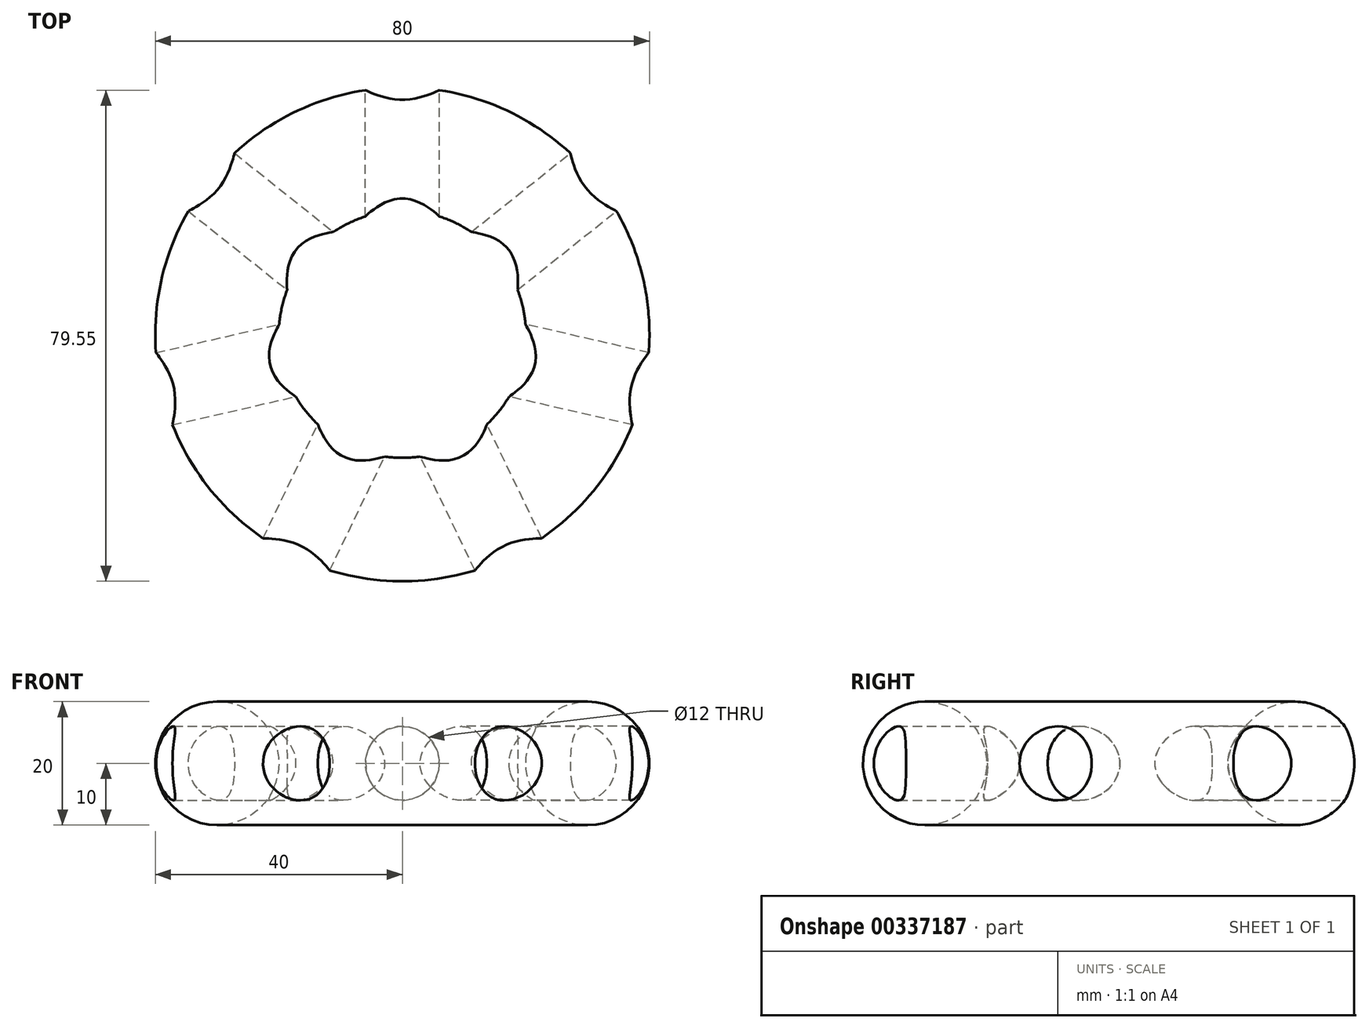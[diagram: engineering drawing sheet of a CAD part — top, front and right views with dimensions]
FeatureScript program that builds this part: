
annotation { "Feature Type Name" : "Feature", "Feature Type Description" : "" }
export const myFeature = defineFeature(function(context is Context, id is Id, definition is map)
    precondition{}
    {
        {
            var Q0;
            Q0=qCreatedBy(makeId("Front.planeOp"),FACE);
            var sketch = newSketch(context, id + "F0", { "sketchPlane" : qUnion([Q0])});
            skCircle(sketch, "E0", {"center": v(-30, 0) * mm, "radius": 10 * mm});
            skLineSegment(sketch, "E1", {"start": v(0, 0) * mm, "end": v(0, 40) * mm});
            skLineSegment(sketch, "E2", {"start": v(0, 0) * mm, "end": v(0, -40) * mm});
            skSolve(sketch);
        }
        {
            var Q0;
            Q0=makeQuery(id+"F0.imprint","IMPRINT",FACE,{"disambiguationData":[TD([[makeQuery(id+"F0.imprint","IMPRINT",EDGE,{"derivedFrom":sQuery(id+"F0.wireOp",EDGE,"E0")}),1.0]])]});
            var Q1;
            Q1=sQuery(id+"F0.wireOp",EDGE,"E1");
            revolve(context, id + "F1", {"entities" : qUnion([Q0]), "axis" : qUnion([Q1]), "revolveType" : RevolveType.FULL});
        }
        {
            var Q0;
            Q0=qCreatedBy(makeId("Top.planeOp"),FACE);
            var sketch = newSketch(context, id + "F2", { "sketchPlane" : qUnion([Q0])});
            skCircle(sketch, "E3", {"center": v(0, 0) * mm, "radius": 40 * mm});
            skLineSegment(sketch, "E4", {"start": v(0, 40) * mm, "end": v(0, 0) * mm});
            skLineSegment(sketch, "E5.1.0", {"start": v(-31.27, 24.94) * mm, "end": v(0, 0) * mm});
            skLineSegment(sketch, "E5.2.0", {"start": v(-39, -8.9) * mm, "end": v(0, 0) * mm});
            skLineSegment(sketch, "E6.1.3.0", {"start": v(-17.36, -36.04) * mm, "end": v(0, 0) * mm});
            skLineSegment(sketch, "E6.1.4.0", {"start": v(17.36, -36.04) * mm, "end": v(0, 0) * mm});
            skLineSegment(sketch, "E6.1.5.0", {"start": v(39, -8.9) * mm, "end": v(0, 0) * mm});
            skLineSegment(sketch, "E6.1.6.0", {"start": v(31.27, 24.94) * mm, "end": v(0, 0) * mm});
            skLineSegment(sketch, "E7.bottom", {"start": v(0, 40) * mm, "end": v(-6, 40) * mm});
            skLineSegment(sketch, "E7.top", {"start": v(0, 15) * mm, "end": v(-6, 15) * mm});
            skLineSegment(sketch, "E7.left", {"start": v(0, 40) * mm, "end": v(0, 15) * mm});
            skLineSegment(sketch, "E7.right", {"start": v(-6, 40) * mm, "end": v(-6, 15) * mm});
            skLineSegment(sketch, "E8.bottom", {"start": v(0, 40) * mm, "end": v(6, 40) * mm});
            skLineSegment(sketch, "E8.top", {"start": v(0, 15) * mm, "end": v(6, 15) * mm});
            skLineSegment(sketch, "E8.right", {"start": v(6, 40) * mm, "end": v(6, 15) * mm});
            skLineSegment(sketch, "E9.1.0", {"start": v(-27.53, 29.63) * mm, "end": v(-7.99, 14.04) * mm});
            skLineSegment(sketch, "E9.2.0", {"start": v(-40.33, -3.05) * mm, "end": v(-15.96, 2.51) * mm});
            skLineSegment(sketch, "E10.2.3.0", {"start": v(-22.76, -33.44) * mm, "end": v(-11.91, -10.91) * mm});
            skLineSegment(sketch, "E10.2.4.0", {"start": v(11.95, -38.64) * mm, "end": v(1.1, -16.12) * mm});
            skLineSegment(sketch, "E10.2.5.0", {"start": v(37.66, -14.75) * mm, "end": v(13.29, -9.19) * mm});
            skLineSegment(sketch, "E10.2.6.0", {"start": v(35.01, 20.25) * mm, "end": v(15.47, 4.66) * mm});
            skLineSegment(sketch, "E11", {"start": v(-27.53, 29.63) * mm, "end": v(-31.27, 24.94) * mm});
            skLineSegment(sketch, "E12", {"start": v(-7.99, 14.04) * mm, "end": v(-11.73, 9.35) * mm});
            skLineSegment(sketch, "E13", {"start": v(-15.96, 2.51) * mm, "end": v(-14.62, -3.34) * mm});
            skLineSegment(sketch, "E14", {"start": v(-11.91, -10.91) * mm, "end": v(-6.5, -13.51) * mm});
            skLineSegment(sketch, "E15", {"start": v(1.1, -16.12) * mm, "end": v(6.5, -13.51) * mm});
            skLineSegment(sketch, "E16", {"start": v(13.29, -9.19) * mm, "end": v(14.62, -3.34) * mm});
            skLineSegment(sketch, "E17", {"start": v(15.47, 4.66) * mm, "end": v(11.73, 9.35) * mm});
            skLineSegment(sketch, "E18", {"start": v(37.66, -14.75) * mm, "end": v(39, -8.9) * mm});
            skLineSegment(sketch, "E19", {"start": v(35.01, 20.25) * mm, "end": v(31.27, 24.94) * mm});
            skLineSegment(sketch, "E20", {"start": v(-39, -8.9) * mm, "end": v(-40.33, -3.05) * mm});
            skLineSegment(sketch, "E21", {"start": v(-17.36, -36.04) * mm, "end": v(-22.76, -33.44) * mm});
            skSolve(sketch);
        }
        {
            var Q0;
            {var subQ3=sQuery(id+"F2.wireOp",EDGE,"E17");Q0=makeQuery(id+"F2.imprint","IMPRINT",FACE,{"disambiguationData":[TD([[makeQuery(id+"F2.imprint","IMPRINT",EDGE,{"derivedFrom":subQ3}),-1.0]])]});}
            var Q1;
            Q1=sQuery(id+"F2.wireOp",EDGE,"E6.1.6.0");
            revolve(context, id + "F3", {"operationType" : NewBodyOperationType.REMOVE, "entities" : qUnion([Q0]), "axis" : qUnion([Q1]), "revolveType" : RevolveType.FULL});
        }
        {
            var Q0;
            {var subQ4=sQuery(id+"F2.wireOp",EDGE,"E8.top");Q0=makeQuery(id+"F2.imprint","IMPRINT",FACE,{"disambiguationData":[TD([[makeQuery(id+"F2.imprint","IMPRINT",EDGE,{"derivedFrom":subQ4}),1.0]])]});}
            var Q1;
            Q1=sQuery(id+"F2.wireOp",EDGE,"E4");
            revolve(context, id + "F4", {"operationType" : NewBodyOperationType.REMOVE, "entities" : qUnion([Q0]), "axis" : qUnion([Q1]), "revolveType" : RevolveType.FULL});
        }
        {
            var Q0;
            {var subQ3=sQuery(id+"F2.wireOp",EDGE,"E12");Q0=makeQuery(id+"F2.imprint","IMPRINT",FACE,{"disambiguationData":[TD([[makeQuery(id+"F2.imprint","IMPRINT",EDGE,{"derivedFrom":subQ3}),-1.0]])]});}
            var Q1;
            Q1=sQuery(id+"F2.wireOp",EDGE,"E5.1.0");
            revolve(context, id + "F5", {"operationType" : NewBodyOperationType.REMOVE, "entities" : qUnion([Q0]), "axis" : qUnion([Q1]), "revolveType" : RevolveType.FULL, "oppositeDirection" : true});
        }
        {
            var Q0;
            {var subQ3=sQuery(id+"F2.wireOp",EDGE,"E13");Q0=makeQuery(id+"F2.imprint","IMPRINT",FACE,{"disambiguationData":[TD([[makeQuery(id+"F2.imprint","IMPRINT",EDGE,{"derivedFrom":subQ3}),-1.0]])]});}
            var Q1;
            Q1=sQuery(id+"F2.wireOp",EDGE,"E5.2.0");
            revolve(context, id + "F6", {"operationType" : NewBodyOperationType.REMOVE, "entities" : qUnion([Q0]), "axis" : qUnion([Q1]), "revolveType" : RevolveType.FULL, "oppositeDirection" : true});
        }
        {
            var Q0;
            {var subQ3=sQuery(id+"F2.wireOp",EDGE,"E14");Q0=makeQuery(id+"F2.imprint","IMPRINT",FACE,{"disambiguationData":[TD([[makeQuery(id+"F2.imprint","IMPRINT",EDGE,{"derivedFrom":subQ3}),-1.0]])]});}
            var Q1;
            Q1=sQuery(id+"F2.wireOp",EDGE,"E6.1.3.0");
            revolve(context, id + "F7", {"operationType" : NewBodyOperationType.REMOVE, "entities" : qUnion([Q0]), "axis" : qUnion([Q1]), "revolveType" : RevolveType.FULL, "oppositeDirection" : true});
        }
        {
            var Q0;
            {var subQ3=sQuery(id+"F2.wireOp",EDGE,"E15");Q0=makeQuery(id+"F2.imprint","IMPRINT",FACE,{"disambiguationData":[TD([[makeQuery(id+"F2.imprint","IMPRINT",EDGE,{"derivedFrom":subQ3}),-1.0]])]});}
            var Q1;
            Q1=sQuery(id+"F2.wireOp",EDGE,"E6.1.4.0");
            revolve(context, id + "F8", {"operationType" : NewBodyOperationType.REMOVE, "entities" : qUnion([Q0]), "axis" : qUnion([Q1]), "revolveType" : RevolveType.FULL, "oppositeDirection" : true});
        }
        {
            var Q0;
            {var subQ3=sQuery(id+"F2.wireOp",EDGE,"E16");Q0=makeQuery(id+"F2.imprint","IMPRINT",FACE,{"disambiguationData":[TD([[makeQuery(id+"F2.imprint","IMPRINT",EDGE,{"derivedFrom":subQ3}),-1.0]])]});}
            var Q1;
            Q1=sQuery(id+"F2.wireOp",EDGE,"E6.1.5.0");
            revolve(context, id + "F9", {"operationType" : NewBodyOperationType.REMOVE, "entities" : qUnion([Q0]), "axis" : qUnion([Q1]), "revolveType" : RevolveType.FULL, "oppositeDirection" : true});
        }
    });
